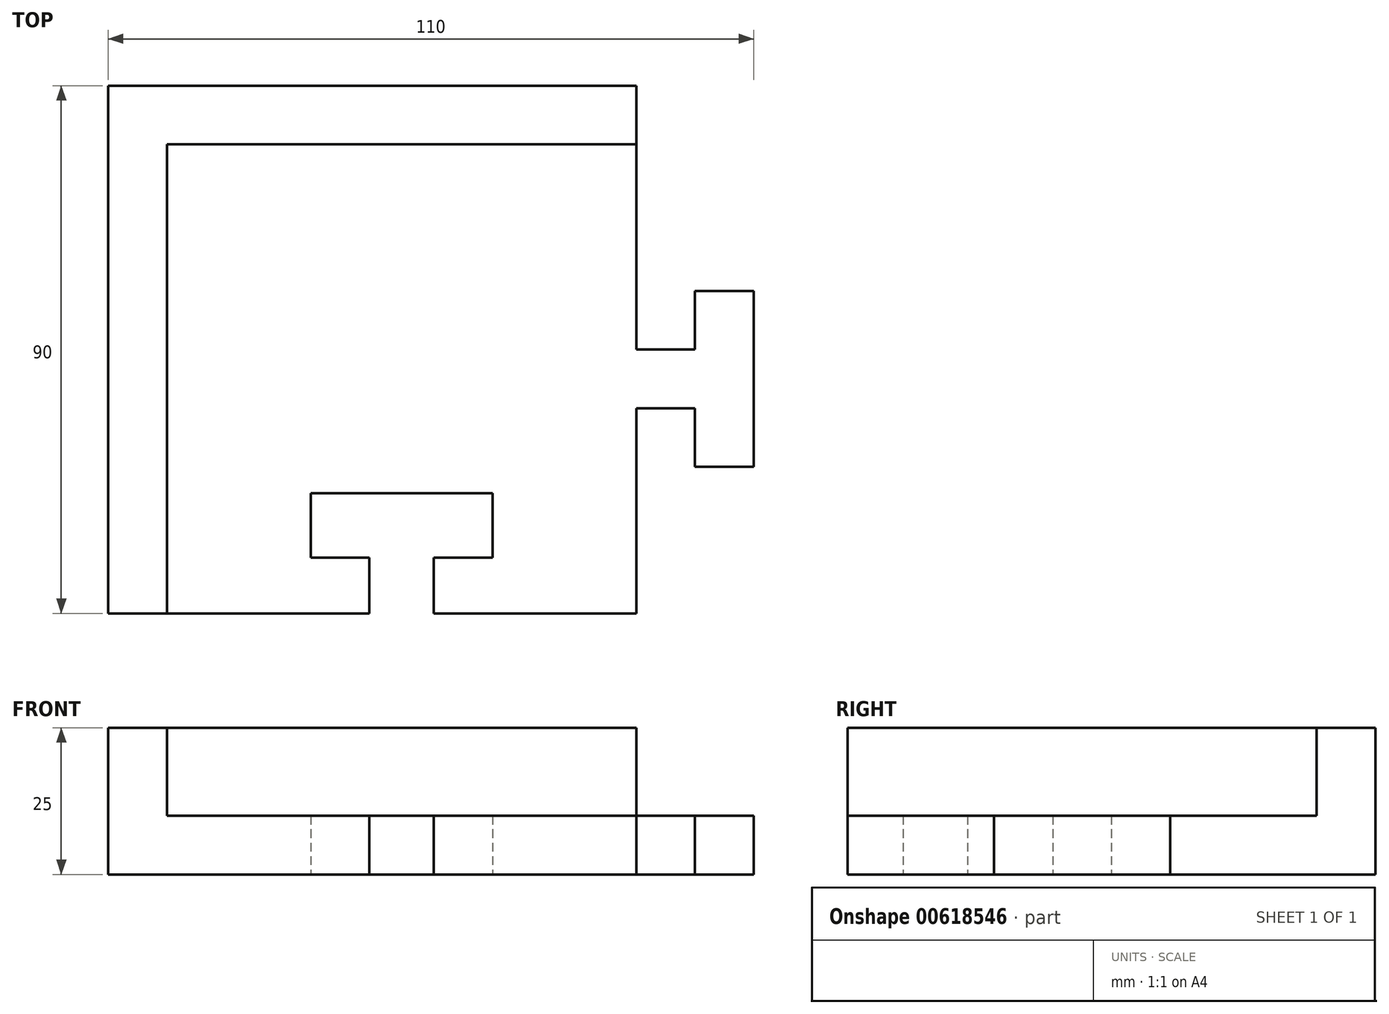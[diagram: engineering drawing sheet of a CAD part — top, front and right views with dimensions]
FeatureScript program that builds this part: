
annotation { "Feature Type Name" : "Feature", "Feature Type Description" : "" }
export const myFeature = defineFeature(function(context is Context, id is Id, definition is map)
    precondition{}
    {
        {
            var Q0;
            Q0=qCreatedBy(makeId("Top.planeOp"),FACE);
            var sketch = newSketch(context, id + "F0", { "sketchPlane" : qUnion([Q0])});
            skLineSegment(sketch, "E0.bottom", {"start": v(0, 0) * mm, "end": v(34.5, 0) * mm});
            skLineSegment(sketch, "E0.top", {"start": v(0, 80) * mm, "end": v(80, 80) * mm});
            skLineSegment(sketch, "E0.left", {"start": v(0, 0) * mm, "end": v(0, 80) * mm});
            skLineSegment(sketch, "E0.right", {"start": v(80, 0) * mm, "end": v(80, 35) * mm});
            skLineSegment(sketch, "E1", {"start": v(80, 45) * mm, "end": v(90, 45) * mm});
            skLineSegment(sketch, "E2", {"start": v(90, 45) * mm, "end": v(90, 55) * mm});
            skLineSegment(sketch, "E3", {"start": v(90, 55) * mm, "end": v(100, 55) * mm});
            skLineSegment(sketch, "E4", {"start": v(100, 55) * mm, "end": v(100, 25) * mm});
            skLineSegment(sketch, "E5", {"start": v(100, 25) * mm, "end": v(90, 25) * mm});
            skLineSegment(sketch, "E6", {"start": v(90, 25) * mm, "end": v(90, 35) * mm});
            skLineSegment(sketch, "E7", {"start": v(90, 35) * mm, "end": v(80, 35) * mm});
            skLineSegment(sketch, "E8.trimOffspring", {"start": v(80, 45) * mm, "end": v(80, 80) * mm});
            skPoint(sketch, "E9.center", {"position": v(40, 40) * mm});
            skPoint(sketch, "E9.1.1.start.orphan", {"position": v(45, 0) * mm});
            skLineSegment(sketch, "E10.trimOffspring", {"start": v(45.5, 0) * mm, "end": v(80, 0) * mm});
            skLineSegment(sketch, "E11.0", {"start": v(34.5, 9.5) * mm, "end": v(34.5, 0) * mm});
            skLineSegment(sketch, "E11.1", {"start": v(24.5, 9.5) * mm, "end": v(34.5, 9.5) * mm});
            skLineSegment(sketch, "E11.2", {"start": v(24.5, 20.5) * mm, "end": v(24.5, 9.5) * mm});
            skLineSegment(sketch, "E11.3", {"start": v(45.5, 0) * mm, "end": v(45.5, 9.5) * mm});
            skLineSegment(sketch, "E11.4", {"start": v(45.5, 9.5) * mm, "end": v(55.5, 9.5) * mm});
            skLineSegment(sketch, "E11.5", {"start": v(55.5, 9.5) * mm, "end": v(55.5, 20.5) * mm});
            skLineSegment(sketch, "E11.6", {"start": v(55.5, 20.5) * mm, "end": v(24.5, 20.5) * mm});
            skPoint(sketch, "E12.MirrorCS.end.orphan", {"position": v(25, 10) * mm});
            skPoint(sketch, "E13.MirrorCS.end.orphan", {"position": v(45, 10) * mm});
            skPoint(sketch, "E14.MirrorCS.end.orphan", {"position": v(55, 10) * mm});
            skPoint(sketch, "E15.MirrorCS.end.orphan", {"position": v(55, 20) * mm});
            skPoint(sketch, "E16.MirrorCS.end.orphan", {"position": v(25, 20) * mm});
            skPoint(sketch, "E9.anchor2.end.orphan", {"position": v(35, 0) * mm});
            skLineSegment(sketch, "E17.0", {"start": v(-10, 90) * mm, "end": v(80, 90) * mm});
            skLineSegment(sketch, "E17.1", {"start": v(-10, 0) * mm, "end": v(-10, 90) * mm});
            skLineSegment(sketch, "E18", {"start": v(80, 90) * mm, "end": v(80, 80) * mm});
            skLineSegment(sketch, "E19", {"start": v(-10, 0) * mm, "end": v(0, 0) * mm});
            skPoint(sketch, "E20.orphan", {"position": v(80, 91.72) * mm});
            skSolve(sketch);
        }
        {
            var Q0;
            Q0=makeQuery(id+"F0.imprint","IMPRINT",FACE,{"disambiguationData":[TD([[makeQuery(id+"F0.imprint","IMPRINT",EDGE,{"derivedFrom":sQuery(id+"F0.wireOp",EDGE,"E0.bottom")}),1.0]])]});
            extrude(context, id + "F1", {"entities" : qUnion([Q0]), "depth" : 10 * mm, "offsetDistance" : 25 * mm});
        }
        {
            var Q0;
            Q0=makeQuery(id+"F0.imprint","IMPRINT",FACE,{"disambiguationData":[TD([[makeQuery(id+"F0.imprint","IMPRINT",EDGE,{"derivedFrom":sQuery(id+"F0.wireOp",EDGE,"E0.top")}),1.0]])]});
            extrude(context, id + "F2", {"entities" : qUnion([Q0]), "operationType" : NewBodyOperationType.ADD, "depth" : 25 * mm, "offsetDistance" : 25 * mm});
        }
    });
